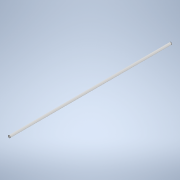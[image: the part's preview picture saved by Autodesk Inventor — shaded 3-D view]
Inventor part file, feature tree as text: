
AUTODESK INVENTOR PART (.ipt)
format: ipt  version: 2020.3 (Build 243373000, 373)  size: 89,600 bytes
history: native  units: mm
features: extrude x1, sketch x1
ambient origin geometry x8: Origin, YZ Plane, XZ Plane, XY Plane, X Axis, Y Axis, Z Axis, Center Point
bodies: Solid1 (feature_tree)
feature tree (2):
  extrude  "Extrusion1"  Depth=180.0mm TaperAngle=0.0deg
  sketch  "Sketch1"  dims[d0=2.5mm d1=180.0mm d2=0.0mm]
